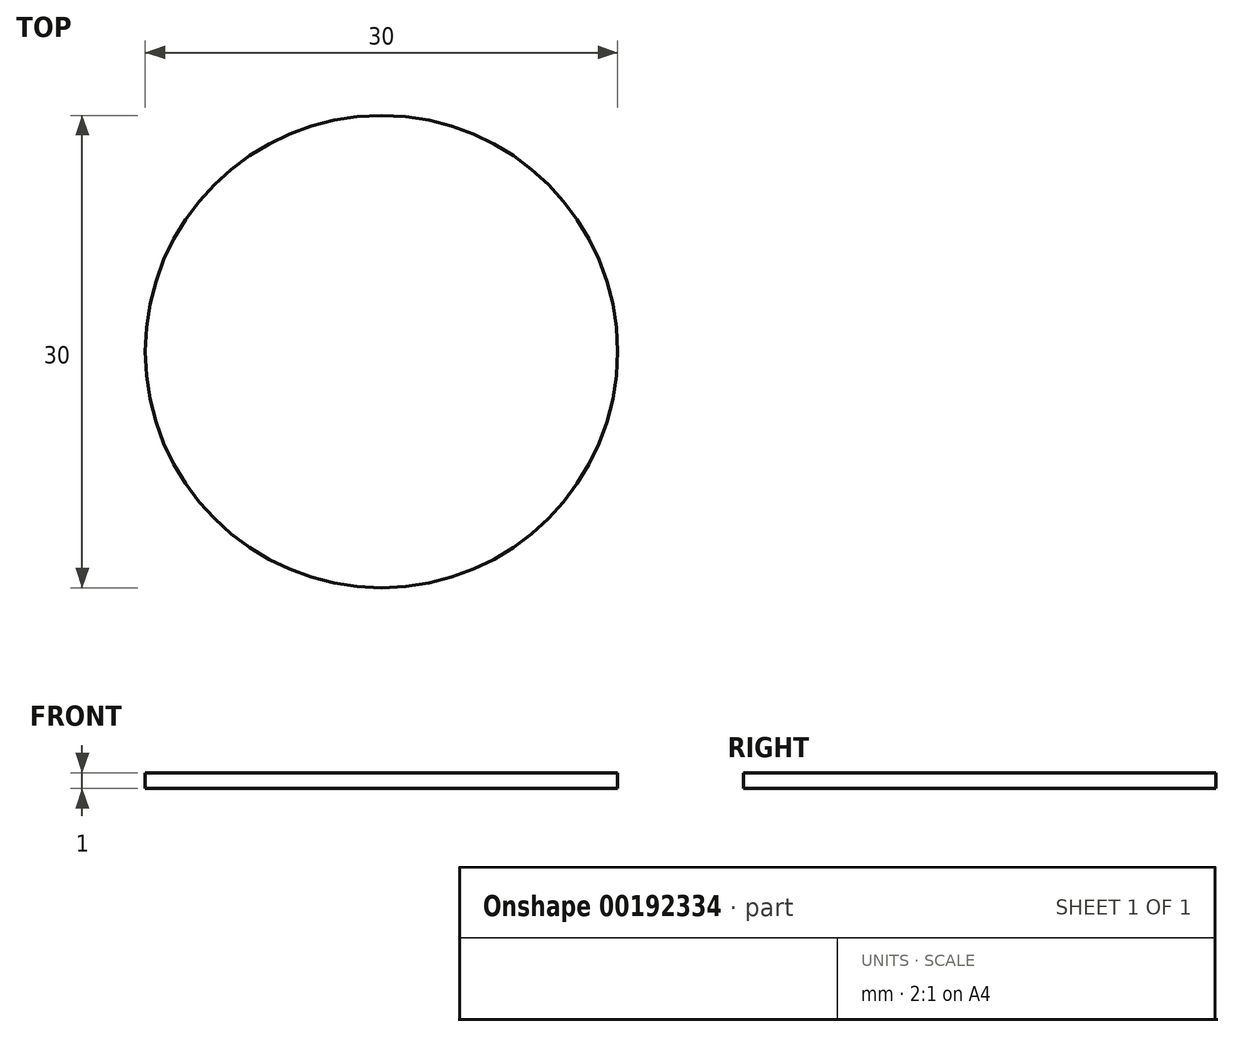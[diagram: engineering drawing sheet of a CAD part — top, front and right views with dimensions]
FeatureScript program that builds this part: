
annotation { "Feature Type Name" : "Feature", "Feature Type Description" : "" }
export const myFeature = defineFeature(function(context is Context, id is Id, definition is map)
    precondition{}
    {
        {
            var Q0;
            Q0=qCreatedBy(makeId("Top.planeOp"),FACE);
            var sketch = newSketch(context, id + "F0", { "sketchPlane" : qUnion([Q0])});
            skCircle(sketch, "E0", {"center": v(0, 0) * mm, "radius": 15 * mm});
            skSolve(sketch);
        }
        {
            var Q0;
            Q0=makeQuery(id+"F0.imprint","IMPRINT",FACE,{"disambiguationData":[TD([[makeQuery(id+"F0.imprint","IMPRINT",EDGE,{"derivedFrom":sQuery(id+"F0.wireOp",EDGE,"E0")}),1.0]])]});
            extrude(context, id + "F1", {"entities" : qUnion([Q0]), "depth" : 1 * mm});
        }
    });
